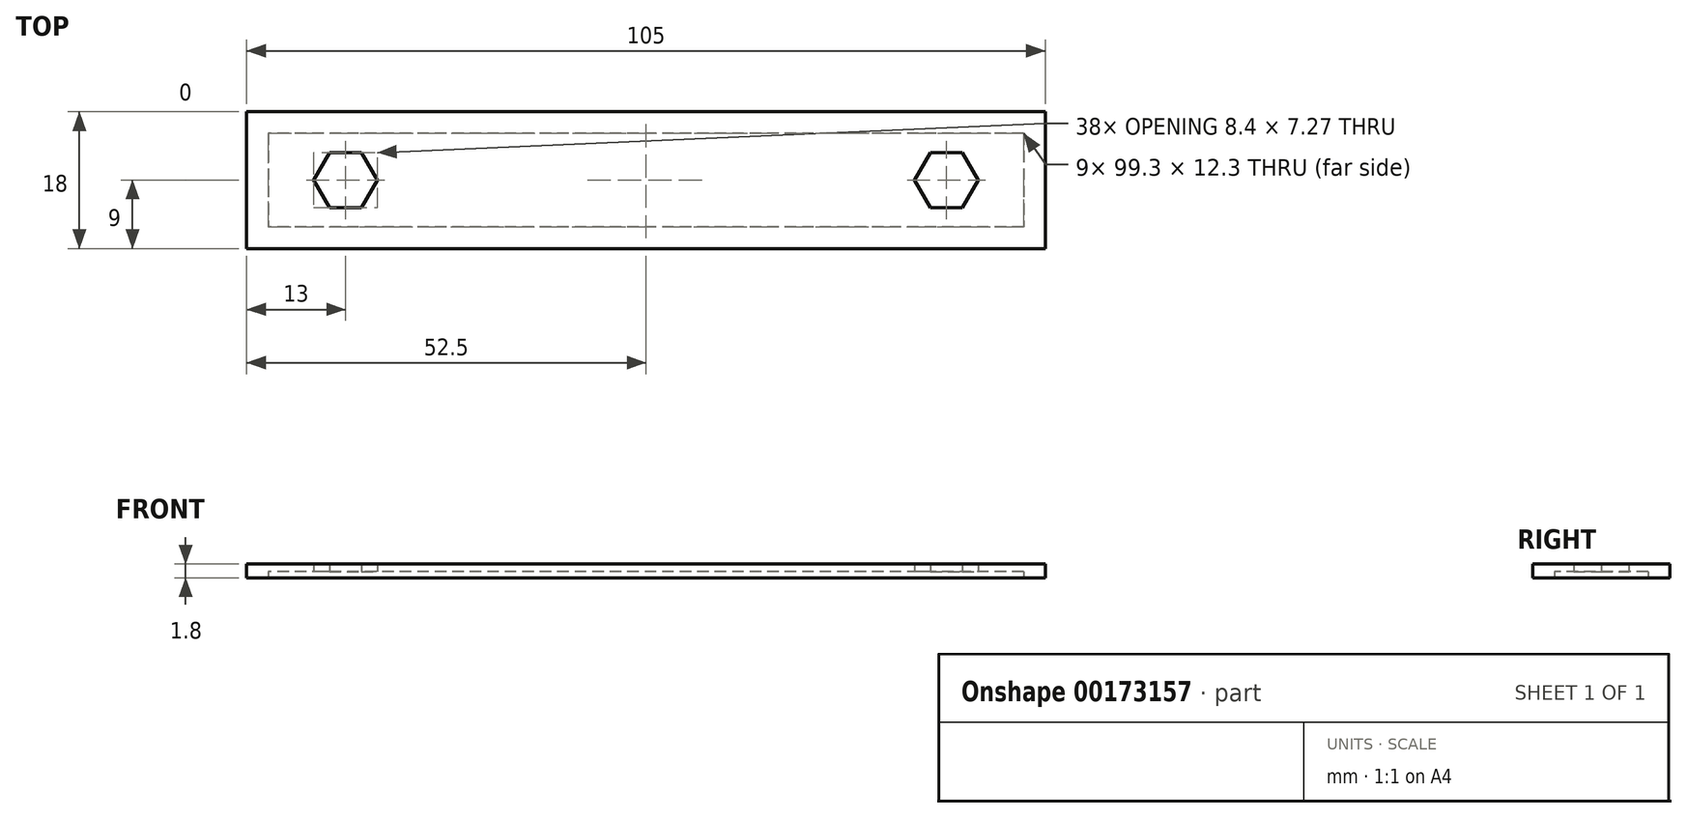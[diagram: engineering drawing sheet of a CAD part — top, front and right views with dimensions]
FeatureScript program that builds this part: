
annotation { "Feature Type Name" : "Feature", "Feature Type Description" : "" }
export const myFeature = defineFeature(function(context is Context, id is Id, definition is map)
    precondition{}
    {
        {
            var Q0;
            Q0=qCreatedBy(makeId("Top.planeOp"),FACE);
            var sketch = newSketch(context, id + "F0", { "sketchPlane" : qUnion([Q0])});
            skLineSegment(sketch, "E0.bottom", {"start": v(49.65, 6.15) * mm, "end": v(-49.65, 6.15) * mm});
            skLineSegment(sketch, "E0.top", {"start": v(49.65, -6.15) * mm, "end": v(-49.65, -6.15) * mm});
            skLineSegment(sketch, "E0.left", {"start": v(49.65, 6.15) * mm, "end": v(49.65, -6.15) * mm});
            skLineSegment(sketch, "E0.right", {"start": v(-49.65, 6.15) * mm, "end": v(-49.65, -6.15) * mm});
            skPoint(sketch, "E0.middle", {"position": v(0, 0) * mm});
            skPoint(sketch, "E1.centerSnap0", {"position": v(49.65, 0) * mm});
            skPoint(sketch, "E2.center.orphan", {"position": v(39.5, 0) * mm});
            skPoint(sketch, "E3.center.orphan", {"position": v(-39.5, 0) * mm});
            skLineSegment(sketch, "E4.bottom", {"start": v(52.5, 9) * mm, "end": v(-52.5, 9) * mm});
            skLineSegment(sketch, "E4.top", {"start": v(52.5, -9) * mm, "end": v(-52.5, -9) * mm});
            skLineSegment(sketch, "E4.left", {"start": v(52.5, 9) * mm, "end": v(52.5, -9) * mm});
            skLineSegment(sketch, "E4.right", {"start": v(-52.5, 9) * mm, "end": v(-52.5, -9) * mm});
            skLineSegment(sketch, "E5", {"start": v(35.3, 0) * mm, "end": v(37.4, 3.64) * mm});
            skLineSegment(sketch, "E6", {"start": v(37.4, 3.64) * mm, "end": v(41.6, 3.64) * mm});
            skLineSegment(sketch, "E7", {"start": v(41.6, 3.64) * mm, "end": v(43.7, 0) * mm});
            skLineSegment(sketch, "E8", {"start": v(43.7, 0) * mm, "end": v(41.6, -3.64) * mm});
            skLineSegment(sketch, "E9", {"start": v(41.6, -3.64) * mm, "end": v(37.4, -3.64) * mm});
            skLineSegment(sketch, "E10", {"start": v(37.4, -3.64) * mm, "end": v(35.3, 0) * mm});
            skLineSegment(sketch, "E11", {"start": v(-43.7, 0) * mm, "end": v(-41.6, 3.64) * mm});
            skLineSegment(sketch, "E12", {"start": v(-41.6, 3.64) * mm, "end": v(-37.4, 3.64) * mm});
            skLineSegment(sketch, "E13", {"start": v(-37.4, 3.64) * mm, "end": v(-35.3, 0) * mm});
            skLineSegment(sketch, "E14", {"start": v(-35.3, 0) * mm, "end": v(-37.4, -3.64) * mm});
            skLineSegment(sketch, "E15", {"start": v(-37.4, -3.64) * mm, "end": v(-41.6, -3.64) * mm});
            skLineSegment(sketch, "E16", {"start": v(-41.6, -3.64) * mm, "end": v(-43.7, 0) * mm});
            skSolve(sketch);
        }
        {
            var Q0;
            Q0=makeQuery(id+"F0.imprint","IMPRINT",FACE,{"disambiguationData":[TD([[makeQuery(id+"F0.imprint","IMPRINT",EDGE,{"derivedFrom":sQuery(id+"F0.wireOp",EDGE,"E0.bottom")}),1.0]])]});
            var Q1;
            Q1=makeQuery(id+"F0.imprint","IMPRINT",FACE,{"disambiguationData":[TD([[makeQuery(id+"F0.imprint","IMPRINT",EDGE,{"derivedFrom":sQuery(id+"F0.wireOp",EDGE,"E0.bottom")}),-1.0]])]});
            extrude(context, id + "F1", {"entities" : qUnion([Q0, Q1]), "depth" : 1.8 * mm});
        }
        {
            var Q0;
            Q0=makeQuery(id+"F0.imprint","IMPRINT",FACE,{"disambiguationData":[TD([[makeQuery(id+"F0.imprint","IMPRINT",EDGE,{"derivedFrom":sQuery(id+"F0.wireOp",EDGE,"E0.bottom")}),1.0]])]});
            extrude(context, id + "F2", {"entities" : qUnion([Q0]), "operationType" : NewBodyOperationType.REMOVE, "depth" : 0.8 * mm});
        }
    });
